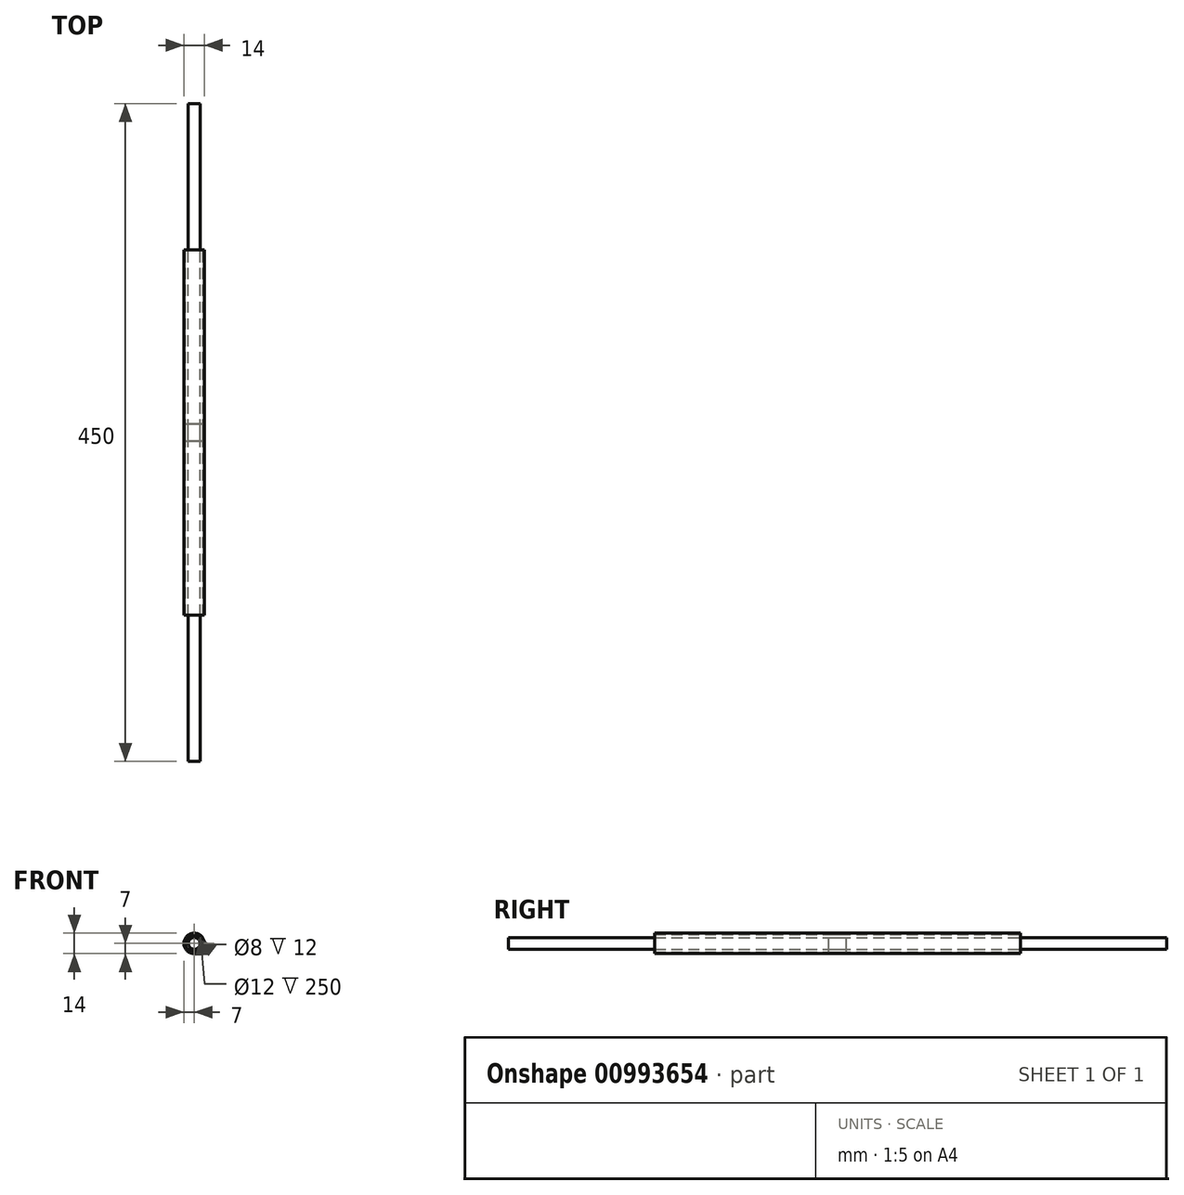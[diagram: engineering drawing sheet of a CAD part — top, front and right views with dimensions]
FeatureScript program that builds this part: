
annotation { "Feature Type Name" : "Feature", "Feature Type Description" : "" }
export const myFeature = defineFeature(function(context is Context, id is Id, definition is map)
    precondition{}
    {
        {
            var Q0;
            Q0=qCreatedBy(makeId("Front.planeOp"),FACE);
            var sketch = newSketch(context, id + "F0", { "sketchPlane" : qUnion([Q0])});
            skCircle(sketch, "E0", {"center": v(0, 0) * mm, "radius": 4 * mm});
            skCircle(sketch, "E1", {"center": v(0, 0) * mm, "radius": 6 * mm});
            skCircle(sketch, "E2", {"center": v(0, 0) * mm, "radius": 7 * mm});
            skSolve(sketch);
        }
        {
            var Q0;
            Q0=makeQuery(id+"F0.imprint","IMPRINT",FACE,{"disambiguationData":[TD([[makeQuery(id+"F0.imprint","IMPRINT",EDGE,{"derivedFrom":sQuery(id+"F0.wireOp",EDGE,"E0")}),1.0]])]});
            extrude(context, id + "F1", {"entities" : qUnion([Q0]), "endBound" : BoundingType.SYMMETRIC, "depth" : 450 * mm, "offsetDistance" : 25 * mm});
        }
        {
            var Q0;
            Q0=makeQuery(id+"F0.imprint","IMPRINT",FACE,{"disambiguationData":[TD([[makeQuery(id+"F0.imprint","IMPRINT",EDGE,{"derivedFrom":sQuery(id+"F0.wireOp",EDGE,"E0")}),-1.0]])]});
            extrude(context, id + "F2", {"entities" : qUnion([Q0]), "endBound" : BoundingType.SYMMETRIC, "depth" : 12 * mm, "offsetDistance" : 25 * mm});
        }
        {
            var Q0;
            Q0=makeQuery(id+"F0.imprint","IMPRINT",FACE,{"disambiguationData":[TD([[makeQuery(id+"F0.imprint","IMPRINT",EDGE,{"derivedFrom":sQuery(id+"F0.wireOp",EDGE,"E1")}),-1.0]])]});
            extrude(context, id + "F3", {"entities" : qUnion([Q0]), "endBound" : BoundingType.SYMMETRIC, "depth" : 250 * mm, "offsetDistance" : 25 * mm});
        }
    });
